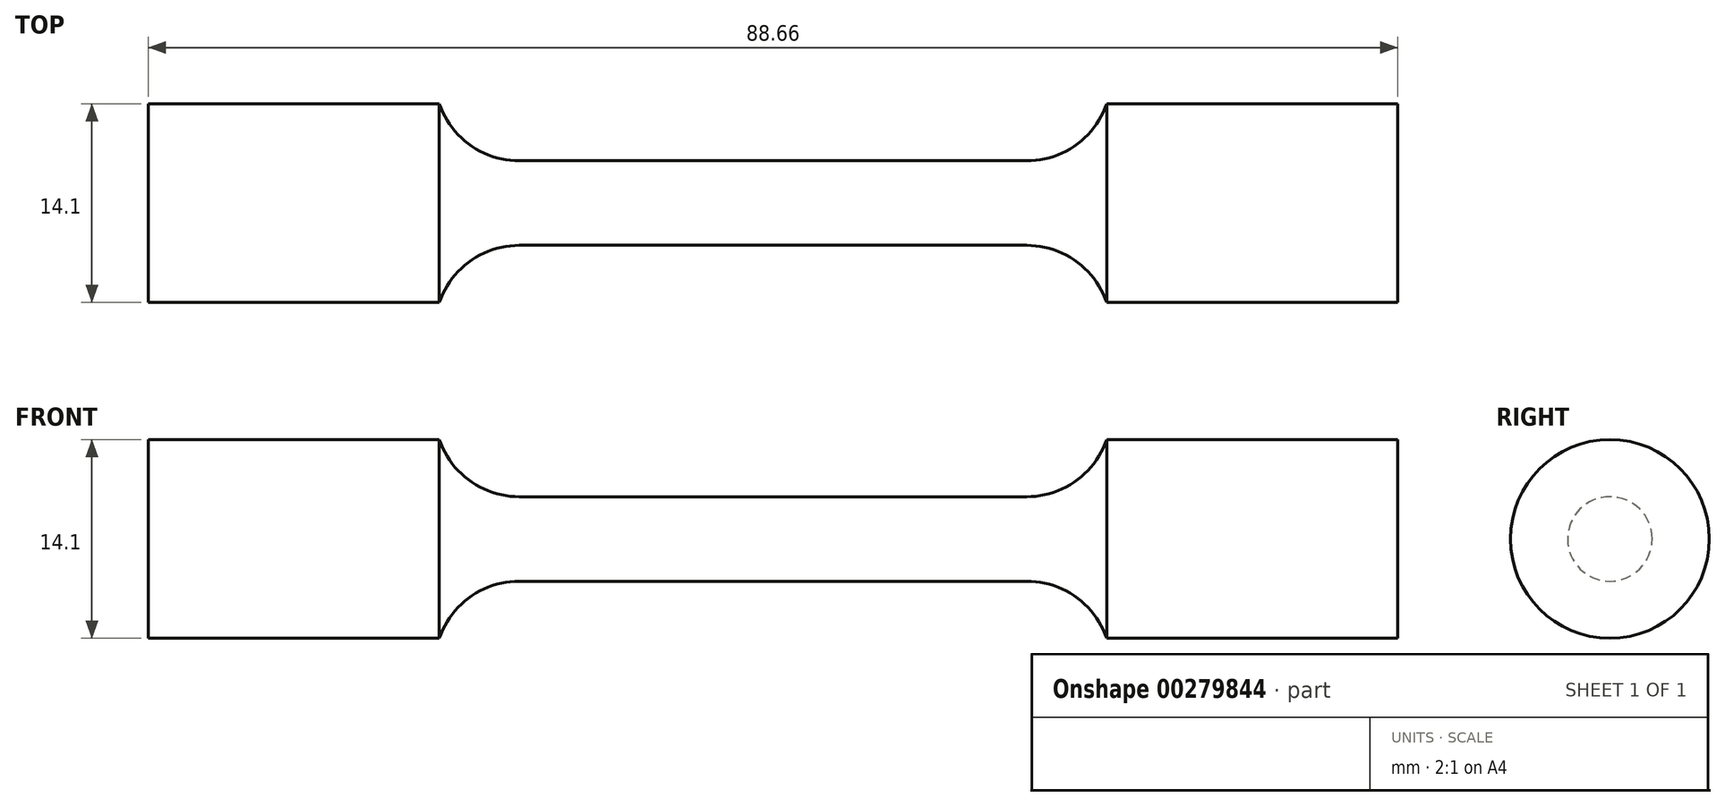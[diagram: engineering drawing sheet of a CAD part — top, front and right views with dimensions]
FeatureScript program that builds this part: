
annotation { "Feature Type Name" : "Feature", "Feature Type Description" : "" }
export const myFeature = defineFeature(function(context is Context, id is Id, definition is map)
    precondition{}
    {
        {
            var Q0;
            Q0=qCreatedBy(makeId("Front.planeOp"),FACE);
            var sketch = newSketch(context, id + "F0", { "sketchPlane" : qUnion([Q0])});
            skLineSegment(sketch, "E0", {"start": v(0, 3) * mm, "end": v(18, 3) * mm});
            skArc(sketch, "E1", {"start": v(18, 3) * mm, "mid": v(21.49, 4.12) * mm, "end": v(23.68, 7.05) * mm});
            skLineSegment(sketch, "E2", {"start": v(23.68, 7.05) * mm, "end": v(44.33, 7.05) * mm});
            skLineSegment(sketch, "E3", {"start": v(44.33, 7.05) * mm, "end": v(44.33, 0) * mm});
            skLineSegment(sketch, "E4.MirrorCS", {"start": v(0, 3) * mm, "end": v(-18, 3) * mm});
            skLineSegment(sketch, "E5.MirrorCS", {"start": v(-23.68, 7.05) * mm, "end": v(-44.33, 7.05) * mm});
            skArc(sketch, "E6.MirrorCS", {"start": v(-18, 3) * mm, "mid": v(-21.49, 4.12) * mm, "end": v(-23.68, 7.05) * mm});
            skLineSegment(sketch, "E7.MirrorCS", {"start": v(-44.33, 7.05) * mm, "end": v(-44.33, 0) * mm});
            skLineSegment(sketch, "E8", {"start": v(-44.33, 0) * mm, "end": v(44.33, 0) * mm});
            skSolve(sketch);
        }
        {
            var Q0;
            Q0=makeQuery(id+"F0.imprint","IMPRINT",FACE,{"disambiguationData":[TD([[makeQuery(id+"F0.imprint","IMPRINT",EDGE,{"derivedFrom":sQuery(id+"F0.wireOp",EDGE,"E0")}),-1.0]])]});
            var Q1;
            Q1=sQuery(id+"F0.wireOp",EDGE,"E8");
            revolve(context, id + "F1", {"entities" : qUnion([Q0]), "axis" : qUnion([Q1]), "revolveType" : RevolveType.FULL});
        }
    });
